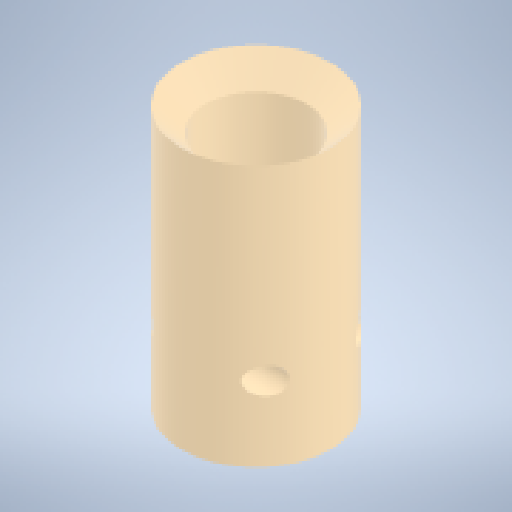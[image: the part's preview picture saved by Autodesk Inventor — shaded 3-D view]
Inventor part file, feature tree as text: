
AUTODESK INVENTOR PART (.ipt)
format: ipt  version: 2024.1 (Build 281209000, 209)  size: 195,072 bytes
history: native  units: in
note: dims shown in document units (in); Inventor stores cm internally (conversion verified against a paired STEP export)
features: hole x2, revolve x1, mirror x1, sketch x1
ambient origin geometry x8: Origin, YZ Plane, XZ Plane, XY Plane, X Axis, Y Axis, Z Axis, Center Point
bodies: Solid1 (feature_tree)
feature tree (5):
  revolve  "Revolution1"  [1 undecoded]
  hole  "Hole2"  [1 undecoded]
  hole  "Hole3"  [1 undecoded]
  mirror  "Mirror1"
  sketch  "Sketch1"  dims[d0=0.245in d1=0.0in d2=1.5in d3=90.0deg d4=0.03in d5=0.325in d6=165.0deg d7=0.5in d8=90.0deg d18=45.0deg d19=0.211in d20=0.25in d21=0.375in d22=0.25in d23=0.5635in d24=0.25in d25=0.0in d28=0.188in d29=0.5in d30=0.188in d31=0.5in d32=90.0deg d33=0.177in d34=0.328in d35=0.119in d36=0.25in d37=0.5635in d38=0.484in d39=0.0in d47=0.3779in d58=0.3388in]
note: 3 required parameter values undecoded (feature->parameter linkage not recoverable at this tier; creation-order binding heuristic only, values carry confidence <= 0.55)